FREECAD ASSEMBLY — COMPONENT RECIPES ("XL30AssemblyChamber01")

This assembly document has 18 components, labeled P0..P17 below (a component is one placed body or linked part). 3 of them carry a construction recipe — the FreeCAD feature program that regenerates the part from scratch, quoted from this document or its linked companion documents; the rest are supplied as boundary geometry only. No exploded tour is included for this assembly.
COMPONENT P0 — geometry summary ("PortAligner_BoughtExternally"; no construction recipe available for this part):
  bounding box: 138.3 x 135.3 x 130.5 mm
  tessellated surface: 227,052 triangles
  volume: 334006 mm^3 (14% of its bounding box)
COMPONENT P1 — recipe-attached ("MainChamberModel", a linked part whose construction recipe lives in a companion FreeCAD document of the same project; that document's serialized recipe follows).
Construction recipe (the companion document, serialized — sketch geometry with constraints, then the solid features built on it; lengths are millimeters unless a unit is written):

FCSTD DOCUMENT  (FreeCAD 0.20R)
Label: XL30MainChamberModel
License: All rights reserved
LicenseURL: http://en.wikipedia.org/wiki/All_rights_reserved
objects: Part::Cylinder×49, Part::Cut×21, Part::Compound×17, Part::MultiFuse×8, Part::Box×7, Part::Sphere×1
note: 103 computed .brp shape members not serialized (recipe doc carries the construction recipe); baked Part::Feature solids carry a one-line shape summary decoded from their .brp

FEATURE [Part::Box] Box  label="Würfel"
  AttacherType = Attacher::AttachEngine3D
  Height = 330
  Length = 330
  Width = 180
FEATURE [Part::Cylinder] Cylinder  label="Zylinder"
  Angle = 360
  AttacherType = Attacher::AttachEngine3D
  FirstAngle = 0
  Height = 180
  Placement = pos=(165,180,165) rot=(1,0,0;1.5708rad)
  Radius = 142
  SecondAngle = 0
FEATURE [Part::Cut] Cut
  Base = -> Box
  Tool = -> Cylinder
FEATURE [Part::Box] Box001  label="Würfel001"
  AttacherType = Attacher::AttachEngine3D
  Height = 50
  Length = 70
  Placement = pos=(0,0,265) rot=(0,-1,0;1.20428rad)
  Width = 180
FEATURE [Part::Cut] Cut001
  Base = -> Cut
  Tool = -> Box001
FEATURE [Part::Cylinder] Cylinder001  label="Flange100Right_Hole"
  Angle = 360
  AttacherType = Attacher::AttachEngine3D
  FirstAngle = 0
  Height = 50
  Placement = pos=(284,107.5,198.5) rot=(0,1,0;1.5708rad)
  Radius = 34.5
  SecondAngle = 0
FEATURE [Part::Cylinder] Cylinder002  label="Flange100Right_Recess"
  Angle = 360
  AttacherType = Attacher::AttachEngine3D
  FirstAngle = 0
  Height = 1
  Placement = pos=(329,107.5,198.5) rot=(0,1,0;1.5708rad)
  Radius = 51.5
  SecondAngle = 0
FEATURE [Part::Cylinder] Cylinder003  label="Zylinder001"
  Angle = 360
  AttacherType = Attacher::AttachEngine3D
  FirstAngle = 0
  Height = 3
  Radius = 41
  SecondAngle = 0
FEATURE [Part::Cylinder] Cylinder004  label="Zylinder002"
  Angle = 360
  AttacherType = Attacher::AttachEngine3D
  FirstAngle = 0
  Height = 3
  Radius = 37
  SecondAngle = 0
FEATURE [Part::Cut] Cut002
  Base = -> Cylinder003
  Placement = pos=(326,107.5,198.5) rot=(0,1,0;1.5708rad)
  Tool = -> Cylinder004
FEATURE [Part::Cylinder] Cylinder005  label="Zylinder003"
  Angle = 360
  AttacherType = Attacher::AttachEngine3D
  FirstAngle = 0
  Height = 10
  Placement = pos=(0,0,-44.3) rot=(0,1,0;1.5708rad)
  Radius = 1.65
  SecondAngle = 0
FEATURE [Part::Cylinder] Cylinder006  label="Zylinder004"
  Angle = 360
  AttacherType = Attacher::AttachEngine3D
  FirstAngle = 0
  Height = 10
  Placement = pos=(0,0,-44.3) rot=(0,1,0;1.5708rad)
  Radius = 1.65
  SecondAngle = 0
FEATURE [Part::Cylinder] Cylinder007  label="Zylinder005"
  Angle = 360
  AttacherType = Attacher::AttachEngine3D
  FirstAngle = 0
  Height = 10
  Placement = pos=(0,0,-44.3) rot=(0,1,0;1.5708rad)
  Radius = 1.65
  SecondAngle = 0
FEATURE [Part::Compound] Compound001
  Links = -> [Cylinder006]
  Placement = pos=(0,0,0) rot=(1,0,0;2.0944rad)
FEATURE [Part::Compound] Compound002
  Links = -> [Cylinder007]
  Placement = pos=(0,0,0) rot=(1,0,0;4.18879rad)
FEATURE [Part::Compound] Compound003  label="M4 holes flange right"
  Links = -> [Cylinder005,Compound001,Compound002]
  Placement = pos=(319,107.5,198.5) rot=(0,0,1;0rad)
FEATURE [Part::MultiFuse] Fusion
  Shapes = -> [Cylinder001,Cylinder002,Cut002,Compound003]
FEATURE [Part::Cut] Cut003
  Base = -> Cut001
  Tool = -> Fusion
FEATURE [Part::Cylinder] Cylinder008  label="Flange120LeftLow_Recess"
  Angle = 360
  AttacherType = Attacher::AttachEngine3D
  FirstAngle = 0
  Height = 1
  Placement = pos=(0,0,-1) rot=(0,0,1;0rad)
  Radius = 61.5
  SecondAngle = 0
FEATURE [Part::Cylinder] Cylinder009  label="Zylinder006"
  Angle = 360
  AttacherType = Attacher::AttachEngine3D
  FirstAngle = 0
  Height = 60
  Placement = pos=(0,0,-45) rot=(0,0,1;0rad)
  Radius = 45
  SecondAngle = 0
FEATURE [Part::Cylinder] Cylinder010  label="Zylinder007"
  Angle = 360
  AttacherType = Attacher::AttachEngine3D
  FirstAngle = 0
  Height = 2
  Placement = pos=(0,0,-3) rot=(0,0,1;0rad)
  Radius = 50
  SecondAngle = 0
FEATURE [Part::Cylinder] Cylinder011  label="Zylinder008"
  Angle = 360
  AttacherType = Attacher::AttachEngine3D
  FirstAngle = 0
  Height = 2
  Placement = pos=(0,0,-3) rot=(0,0,1;0rad)
  Radius = 46
  SecondAngle = 0
FEATURE [Part::Cut] Cut004
  Base = -> Cylinder010
  Tool = -> Cylinder011
FEATURE [Part::Cylinder] Cylinder012  label="Zylinder009"
  Angle = 360
  AttacherType = Attacher::AttachEngine3D
  FirstAngle = 0
  Height = 10
  Placement = pos=(54.5,0,-10) rot=(0,0,1;0rad)
  Radius = 2.5
  SecondAngle = 0
FEATURE [Part::Cylinder] Cylinder013  label="Zylinder010"
  Angle = 360
  AttacherType = Attacher::AttachEngine3D
  FirstAngle = 0
  Height = 10
  Placement = pos=(54.5,0,-10) rot=(0,0,1;0rad)
  Radius = 2.5
  SecondAngle = 0
FEATURE [Part::Cylinder] Cylinder015  label="Zylinder012"
  Angle = 360
  AttacherType = Attacher::AttachEngine3D
  FirstAngle = 0
  Height = 10
  Placement = pos=(54.5,0,-10) rot=(0,0,1;0rad)
  Radius = 2.5
  SecondAngle = 0
FEATURE [Part::Compound] Compound
  Links = -> [Cylinder013]
  Placement = pos=(0,0,0) rot=(0,0,1;2.0944rad)
FEATURE [Part::Compound] Compound004
  Links = -> [Cylinder015]
  Placement = pos=(0,0,0) rot=(0,0,1;4.18879rad)
FEATURE [Part::MultiFuse] Fusion001  label="Flange120LeftLow"
  Placement = pos=(0,115.5,140) rot=(0,-1,0;1.5708rad)
  Shapes = -> [Cylinder008,Cylinder009,Cut004,Cylinder012,Compound,Compound004]
FEATURE [Part::Cut] Cut005
  Base = -> Cut003
  Tool = -> Fusion001
FEATURE [Part::Cylinder] Cylinder016  label="Zylinder013"
  Angle = 360
  AttacherType = Attacher::AttachEngine3D
  FirstAngle = 0
  Height = 100
  Placement = pos=(0,0,0) rot=(0,1,0;1.5708rad)
  Radius = 27
  SecondAngle = 0
FEATURE [Part::Cylinder] Cylinder017  label="Zylinder014"
  Angle = 360
  AttacherType = Attacher::AttachEngine3D
  FirstAngle = 0
  Height = 100
  Placement = pos=(-99,0,0) rot=(0,1,0;1.5708rad)
  Radius = 51.5
  SecondAngle = 0
FEATURE [Part::Cylinder] Cylinder018  label="Zylinder015"
  Angle = 360
  AttacherType = Attacher::AttachEngine3D
  FirstAngle = 0
  Height = 2
  Radius = 41
  SecondAngle = 0
FEATURE [Part::Cylinder] Cylinder019  label="Zylinder016"
  Angle = 360
  AttacherType = Attacher::AttachEngine3D
  FirstAngle = 0
  Height = 2
  Radius = 37
  SecondAngle = 0
FEATURE [Part::Cut] Cut006
  Base = -> Cylinder018
  Placement = pos=(1,0,0) rot=(0,1,0;1.5708rad)
  Tool = -> Cylinder019
FEATURE [Part::Cylinder] Cylinder020  label="Zylinder017"
  Angle = 360
  AttacherType = Attacher::AttachEngine3D
  FirstAngle = 0
  Height = 10
  Placement = pos=(0,0,-44.5) rot=(0,1,0;1.5708rad)
  Radius = 3.3
  SecondAngle = 0
FEATURE [Part::Cylinder] Cylinder021  label="Zylinder018"
  Angle = 360
  AttacherType = Attacher::AttachEngine3D
  FirstAngle = 0
  Height = 10
  Placement = pos=(0,0,-44.5) rot=(0,1,0;1.5708rad)
  Radius = 3.3
  SecondAngle = 0
FEATURE [Part::Cylinder] Cylinder022  label="Zylinder019"
  Angle = 360
  AttacherType = Attacher::AttachEngine3D
  FirstAngle = 0
  Height = 10
  Placement = pos=(0,0,-44.5) rot=(0,1,0;1.5708rad)
  Radius = 3.3
  SecondAngle = 0
FEATURE [Part::Compound] Compound005
  Links = -> [Cylinder021]
  Placement = pos=(0,0,0) rot=(1,0,0;2.0944rad)
FEATURE [Part::Compound] Compound006
  Links = -> [Cylinder022]
  Placement = pos=(0,0,0) rot=(1,0,0;4.18879rad)
FEATURE [Part::MultiFuse] Fusion002  label="FlangeSEDetector"
  Placement = pos=(18,116,275) rot=(0,1,0;0.340339rad)
  Shapes = -> [Cylinder016,Cylinder017,Cut006,Cylinder020,Compound005,Compound006]
FEATURE [Part::Cut] Cut007
  Base = -> Cut005
  Tool = -> Fusion002
FEATURE [Part::Cylinder] Cylinder023  label="ODPHoleNoFlange"
  Angle = 360
  AttacherType = Attacher::AttachEngine3D
  FirstAngle = 0
  Height = 50
  Placement = pos=(125,140,0) rot=(0,0,1;0rad)
  Radius = 40
  SecondAngle = 0
FEATURE [Part::Cut] Cut008
  Base = -> Cut007
  Tool = -> Cylinder023
FEATURE [Part::Cylinder] Cylinder024  label="EGunHoleWithoutFlange"
  Angle = 360
  AttacherType = Attacher::AttachEngine3D
  FirstAngle = 0
  Height = 50
  Placement = pos=(165,120,280) rot=(0,0,1;0rad)
  Radius = 50
  SecondAngle = 0
FEATURE [Part::Cut] Cut009  label="FrontChamber"
  Base = -> Cut008
  Tool = -> Cylinder024
FEATURE [Part::Box] Box002  label="Würfel002"
  AttacherType = Attacher::AttachEngine3D
  Height = 330
  Length = 330
  Width = 105
FEATURE [Part::Box] Box003  label="Würfel003"
  AttacherType = Attacher::AttachEngine3D
  Height = 330
  Length = 150
  Placement = pos=(330,0,0) rot=(0,0,1;0.785398rad)
  Width = 200
FEATURE [Part::Box] Box004  label="Würfel004"
  AttacherType = Attacher::AttachEngine3D
  Height = 150
  Length = 240
  Placement = pos=(90,0,330) rot=(-1,0,0;0.785398rad)
  Width = 150
FEATURE [Part::Box] Box005  label="Würfel005"
  AttacherType = Attacher::AttachEngine3D
  Height = 330
  Length = 150
  Placement = pos=(0,15,0) rot=(0,0,1;0.785398rad)
  Width = 100
FEATURE [Part::Box] Box007  label="Würfel007"
  AttacherType = Attacher::AttachEngine3D
  Height = 50
  Length = 70
  Placement = pos=(0,0,265) rot=(0,-1,0;1.20428rad)
  Width = 180
FEATURE [Part::MultiFuse] Fusion003
  Shapes = -> [Box005,Box003,Box004,Box007]
FEATURE [Part::Cut] Cut010
  Base = -> Box002
  Placement = pos=(0,180,0) rot=(0,0,1;0rad)
  Tool = -> Fusion003
FEATURE [Part::Cylinder] Cylinder025  label="Zylinder020"
  Angle = 360
  AttacherType = Attacher::AttachEngine3D
  FirstAngle = 0
  Height = 100
  Placement = pos=(0,0,0) rot=(0,1,0;1.5708rad)
  Radius = 27
  SecondAngle = 0
FEATURE [Part::Cylinder] Cylinder026  label="Zylinder021"
  Angle = 360
  AttacherType = Attacher::AttachEngine3D
  FirstAngle = 0
  Height = 100
  Placement = pos=(-99,0,0) rot=(0,1,0;1.5708rad)
  Radius = 51.5
  SecondAngle = 0
FEATURE [Part::Cylinder] Cylinder027  label="Zylinder022"
  Angle = 360
  AttacherType = Attacher::AttachEngine3D
  FirstAngle = 0
  Height = 2
  Radius = 41
  SecondAngle = 0
FEATURE [Part::Cylinder] Cylinder028  label="Zylinder023"
  Angle = 360
  AttacherType = Attacher::AttachEngine3D
  FirstAngle = 0
  Height = 2
  Radius = 37
  SecondAngle = 0
FEATURE [Part::Cut] Cut011
  Base = -> Cylinder027
  Placement = pos=(1,0,0) rot=(0,1,0;1.5708rad)
  Tool = -> Cylinder028
FEATURE [Part::Cylinder] Cylinder029  label="Zylinder024"
  Angle = 360
  AttacherType = Attacher::AttachEngine3D
  FirstAngle = 0
  Height = 10
  Placement = pos=(0,0,-44.5) rot=(0,1,0;1.5708rad)
  Radius = 3.3
  SecondAngle = 0
FEATURE [Part::Cylinder] Cylinder030  label="Zylinder025"
  Angle = 360
  AttacherType = Attacher::AttachEngine3D
  FirstAngle = 0
  Height = 10
  Placement = pos=(0,0,-44.5) rot=(0,1,0;1.5708rad)
  Radius = 3.3
  SecondAngle = 0
FEATURE [Part::Compound] Compound007
  Links = -> [Cylinder030]
  Placement = pos=(0,0,0) rot=(1,0,0;2.0944rad)
FEATURE [Part::Cylinder] Cylinder031  label="Zylinder026"
  Angle = 360
  AttacherType = Attacher::AttachEngine3D
  FirstAngle = 0
  Height = 10
  Placement = pos=(0,0,-44.5) rot=(0,1,0;1.5708rad)
  Radius = 3.3
  SecondAngle = 0
FEATURE [Part::Compound] Compound008
  Links = -> [Cylinder031]
  Placement = pos=(0,0,0) rot=(1,0,0;4.18879rad)
FEATURE [Part::MultiFuse] Fusion004  label="BSEFlange"
  Placement = pos=(278.7,231.3,105) rot=(0,0,1;3.92699rad)
  Shapes = -> [Cylinder025,Cylinder026,Cut011,Cylinder029,Compound007,Compound008]
FEATURE [Part::Compound] Compound009  label="BSEFlange1"
  Links = -> [Fusion004]
FEATURE [Part::Cut] Cut012
  Base = -> Cut010
  Tool = -> Compound009
FEATURE [Part::Cylinder] Cylinder032  label="Zylinder027"
  Angle = 360
  AttacherType = Attacher::AttachEngine3D
  FirstAngle = 0
  Height = 100
  Placement = pos=(0,0,0) rot=(0,1,0;1.5708rad)
  Radius = 20
  SecondAngle = 0
FEATURE [Part::Cylinder] Cylinder033  label="Zylinder028"
  Angle = 360
  AttacherType = Attacher::AttachEngine3D
  FirstAngle = 0
  Height = 100
  Placement = pos=(-99,0,0) rot=(0,1,0;1.5708rad)
  Radius = 44
  SecondAngle = 0
FEATURE [Part::Cylinder] Cylinder034  label="Zylinder029"
  Angle = 360
  AttacherType = Attacher::AttachEngine3D
  FirstAngle = 0
  Height = 2
  Radius = 33.8
  SecondAngle = 0
FEATURE [Part::Cylinder] Cylinder035  label="Zylinder030"
  Angle = 360
  AttacherType = Attacher::AttachEngine3D
  FirstAngle = 0
  Height = 2
  Radius = 30
  SecondAngle = 0
FEATURE [Part::Cut] Cut013
  Base = -> Cylinder034
  Placement = pos=(1,0,0) rot=(0,1,0;1.5708rad)
  Tool = -> Cylinder035
FEATURE [Part::Cylinder] Cylinder036  label="Zylinder031"
  Angle = 360
  AttacherType = Attacher::AttachEngine3D
  FirstAngle = 0
  Height = 10
  Placement = pos=(0,0,-37.5) rot=(0,1,0;1.5708rad)
  Radius = 3.3
  SecondAngle = 0
FEATURE [Part::Cylinder] Cylinder037  label="Zylinder032"
  Angle = 360
  AttacherType = Attacher::AttachEngine3D
  FirstAngle = 0
  Height = 10
  Placement = pos=(0,0,-37.5) rot=(0,1,0;1.5708rad)
  Radius = 3.3
  SecondAngle = 0
FEATURE [Part::Compound] Compound010
  Links = -> [Cylinder037]
  Placement = pos=(0,0,0) rot=(1,0,0;2.0944rad)
FEATURE [Part::Cylinder] Cylinder038  label="Zylinder033"
  Angle = 360
  AttacherType = Attacher::AttachEngine3D
  FirstAngle = 0
  Height = 10
  Placement = pos=(0,0,-37.5) rot=(0,1,0;1.5708rad)
  Radius = 3.3
  SecondAngle = 0
FEATURE [Part::Compound] Compound011
  Links = -> [Cylinder038]
  Placement = pos=(0,0,0) rot=(1,0,0;4.18879rad)
FEATURE [Part::MultiFuse] Fusion005  label="BSEFlange003"
  Placement = pos=(0,0,0) rot=(0,0,-1;0.785398rad)
  Shapes = -> [Cylinder032,Cylinder033,Cut013,Cylinder036,Compound010,Compound011]
FEATURE [Part::Compound] Compound012  label="SideFlangeBack2Low"
  Links = -> [Fusion005]
  Placement = pos=(45,240,97.5) rot=(0,0,1;0rad)
FEATURE [Part::Cut] Cut014
  Base = -> Cut012
  Tool = -> Compound012
FEATURE [Part::Cylinder] Cylinder039  label="Zylinder034"
  Angle = 360
  AttacherType = Attacher::AttachEngine3D
  FirstAngle = 0
  Height = 110
  Placement = pos=(-20,0,20) rot=(0,1,0;2.35619rad)
  Radius = 20
  SecondAngle = 0
FEATURE [Part::Cylinder] Cylinder040  label="Zylinder035"
  Angle = 360
  AttacherType = Attacher::AttachEngine3D
  FirstAngle = 0
  Height = 100
  Placement = pos=(-99,0,0) rot=(0,1,0;1.5708rad)
  Radius = 51.5
  SecondAngle = 0
FEATURE [Part::Cylinder] Cylinder041  label="Zylinder036"
  Angle = 360
  AttacherType = Attacher::AttachEngine3D
  FirstAngle = 0
  Height = 2
  Radius = 41
  SecondAngle = 0
FEATURE [Part::Cylinder] Cylinder042  label="Zylinder037"
  Angle = 360
  AttacherType = Attacher::AttachEngine3D
  FirstAngle = 0
  Height = 2
  Radius = 37
  SecondAngle = 0
FEATURE [Part::Cut] Cut015
  Base = -> Cylinder041
  Placement = pos=(1,0,0) rot=(0,1,0;1.5708rad)
  Tool = -> Cylinder042
FEATURE [Part::Cylinder] Cylinder043  label="Zylinder038"
  Angle = 360
  AttacherType = Attacher::AttachEngine3D
  FirstAngle = 0
  Height = 10
  Placement = pos=(0,0,-44.5) rot=(0,1,0;1.5708rad)
  Radius = 3.3
  SecondAngle = 0
FEATURE [Part::Cylinder] Cylinder044  label="Zylinder039"
  Angle = 360
  AttacherType = Attacher::AttachEngine3D
  FirstAngle = 0
  Height = 10
  Placement = pos=(0,0,-44.5) rot=(0,1,0;1.5708rad)
  Radius = 3.3
  SecondAngle = 0
FEATURE [Part::Compound] Compound013
  Links = -> [Cylinder044]
  Placement = pos=(0,0,0) rot=(1,0,0;2.0944rad)
FEATURE [Part::Cylinder] Cylinder045  label="Zylinder040"
  Angle = 360
  AttacherType = Attacher::AttachEngine3D
  FirstAngle = 0
  Height = 10
  Placement = pos=(0,0,-44.5) rot=(0,1,0;1.5708rad)
  Radius = 3.3
  SecondAngle = 0
FEATURE [Part::Compound] Compound014
  Links = -> [Cylinder045]
  Placement = pos=(0,0,0) rot=(1,0,0;4.18879rad)
FEATURE [Part::MultiFuse] Fusion006  label="BSEFlange005"
  Placement = pos=(0,0,286) rot=(0,0,-1;0.785398rad)
  Shapes = -> [Cylinder039,Cylinder040,Cut015,Cylinder043,Compound013,Compound014]
FEATURE [Part::Compound] Compound015  label="BackTopFlange100"
  Links = -> [Fusion006]
  Placement = pos=(45,240,0) rot=(0,0,1;0rad)
FEATURE [Part::Cut] Cut016  label="BackChamber01"
  Base = -> Cut014
  Tool = -> Compound015
FEATURE [Part::Cylinder] Cylinder046  label="Zylinder041"
  Angle = 360
  AttacherType = Attacher::AttachEngine3D
  FirstAngle = 0
  Height = 800
  Placement = pos=(36,500,38) rot=(1,0,0;1.5708rad)
  Radius = 10
  SecondAngle = 0
FEATURE [Part::Cylinder] Cylinder047  label="Zylinder042"
  Angle = 360
  AttacherType = Attacher::AttachEngine3D
  FirstAngle = 0
  Height = 800
  Placement = pos=(302,500,34) rot=(1,0,0;1.5708rad)
  Radius = 10
  SecondAngle = 0
FEATURE [Part::Compound] Compound016
  Links = -> [Cylinder047,Cylinder046]
FEATURE [Part::Sphere] Sphere  label="Kugel"
  Angle1 = -90
  Angle2 = 90
  Angle3 = 360
  AttacherType = Attacher::AttachEngine3D
  Placement = pos=(165,0,165) rot=(0,0,1;0rad)
  Radius = 230
FEATURE [Part::Cut] Cut017
  Base = -> Cut016
  Tool = -> Sphere
FEATURE [Part::MultiFuse] Fusion007
  Shapes = -> [Cut009,Cut017]
FEATURE [Part::Cut] Cut018
  Base = -> Fusion007
  Tool = -> Compound016
FEATURE [Part::Cylinder] Cylinder048  label="Zylinder043"
  Angle = 360
  AttacherType = Attacher::AttachEngine3D
  FirstAngle = 0
  Height = 4
  Radius = 155
  SecondAngle = 0
FEATURE [Part::Cylinder] Cylinder049  label="Zylinder044"
  Angle = 360
  AttacherType = Attacher::AttachEngine3D
  FirstAngle = 0
  Height = 4
  Radius = 151
  SecondAngle = 0
FEATURE [Part::Cut] Cut019
  Base = -> Cylinder048
  Placement = pos=(165,4,165) rot=(1,0,0;1.5708rad)
  Tool = -> Cylinder049
FEATURE [Part::Cut] Cut020  label="MainChamberModel"
  Base = -> Cut018
  Tool = -> Cut019
COMPONENT P2 — geometry summary ("BasicOutline_Part0and1"; no construction recipe available for this part):
  bounding box: 150.0 x 150.0 x 137.0 mm
  tessellated surface: 6,006 triangles
  volume: 950630 mm^3 (31% of its bounding box)
  symmetry: 4-fold rotationally symmetric about the z axis; mirror-symmetric across its x mid-plane, y mid-plane
COMPONENT P3 — recipe-attached ("XL30FinalAppertureHolder", a linked part whose construction recipe lives in a companion FreeCAD document of the same project; that document's serialized recipe follows).
Construction recipe (the companion document, serialized — sketch geometry with constraints, then the solid features built on it; lengths are millimeters unless a unit is written):

FCSTD DOCUMENT  (FreeCAD 0.20R)
Label: XL30FinalAppertureHolder
License: All rights reserved
LicenseURL: http://en.wikipedia.org/wiki/All_rights_reserved
objects: Part::Cylinder×8, Part::MultiFuse×2, Part::Cut×2, PartDesign::AdditiveCylinder×1, PartDesign::Hole×1, PartDesign::Body×1, Part::Feature×1
note: 18 computed .brp shape members not serialized (recipe doc carries the construction recipe); baked Part::Feature solids carry a one-line shape summary decoded from their .brp

FEATURE [Part::Cylinder] Cylinder  label="Zylinder"
  Angle = 360
  AttacherType = Attacher::AttachEngine3D
  FirstAngle = 0
  Height = 0.5
  Radius = 4.5
  SecondAngle = 0
FEATURE [Part::Cylinder] Cylinder001  label="Zylinder001"
  Angle = 360
  AttacherType = Attacher::AttachEngine3D
  FirstAngle = 0
  Height = 0.9
  Radius = 3.5
  SecondAngle = 0
FEATURE [Part::Cylinder] Cylinder002  label="Zylinder002"
  Angle = 360
  AttacherType = Attacher::AttachEngine3D
  FirstAngle = 0
  Height = 3.5
  Radius = 2.5
  SecondAngle = 0
FEATURE [Part::Cylinder] Cylinder003  label="Zylinder003"
  Angle = 360
  AttacherType = Attacher::AttachEngine3D
  FirstAngle = 0
  Height = 4
  Placement = pos=(0,0,3.5) rot=(0,0,1;0rad)
  Radius = 2.4
  SecondAngle = 0
FEATURE [Part::Cylinder] Cylinder004  label="Zylinder004"
  Angle = 360
  AttacherType = Attacher::AttachEngine3D
  FirstAngle = 0
  Height = 10
  Radius = 1.87
  SecondAngle = 0
FEATURE [Part::MultiFuse] Fusion
  Shapes = -> [Cylinder004,Cylinder,Cylinder001,Cylinder002,Cylinder003]
FEATURE [Part::Cylinder] Cylinder005  label="Zylinder005"
  Angle = 360
  AttacherType = Attacher::AttachEngine3D
  FirstAngle = 0
  Height = 100
  Radius = 1.2
  SecondAngle = 0
FEATURE [Part::Cylinder] Cylinder006  label="Zylinder006"
  Angle = 360
  AttacherType = Attacher::AttachEngine3D
  FirstAngle = 0
  Height = 7
  Radius = 2
  SecondAngle = 0
FEATURE [Part::Cylinder] Cylinder007  label="Zylinder007"
  Angle = 360
  AttacherType = Attacher::AttachEngine3D
  FirstAngle = 0
  Height = 10
  Placement = pos=(0,0,8) rot=(0,0,1;0rad)
  Radius = 1.5
  SecondAngle = 0
FEATURE [Part::MultiFuse] Fusion001
  Shapes = -> [Cylinder007,Cylinder005,Cylinder006]
FEATURE [Part::Cut] Cut
  Base = -> Fusion
  Tool = -> Fusion001
FEATURE [PartDesign::AdditiveCylinder] Cylinder008
  Angle = 360
  AttacherType = Attacher::AttachEngine3D
  FirstAngle = 0
  Height = 4
  Radius = 3
  SecondAngle = 0
FEATURE [PartDesign::Hole] Hole
  BaseFeature = -> Cylinder008
  CustomThreadClearance = 0
  Depth = 18.9163
  DepthType = 0
  Diameter = 4.224
  DrillForDepth = false
  DrillPoint = 1
  DrillPointAngle = 118
  HoleCutCountersinkAngle = 90
  HoleCutCustomValues = false
  HoleCutDepth = 0
  HoleCutDiameter = 6.1
  HoleCutType = 0
  ModelThread = true
  Profile = -> Cylinder008 [Face3]
  Tapered = false
  TaperedAngle = 90
  ThreadClass = 0
  ThreadDepth = 18.9163
  ThreadDepthType = 0
  ThreadDirection = 0
  ThreadFit = 0
  ThreadSize = 13
  ThreadType = 1
  Threaded = true
  UseCustomThreadClearance = false
FEATURE [PartDesign::Body] Body  label="ThreadCutterM3"
  Group = -> [Cylinder008,Hole]
  Origin = -> Origin
  Placement = pos=(0,0,3.5) rot=(0,0,1;0rad)
  Tip = -> Hole
FEATURE [Part::Cut] Cut001
  Base = -> Cut
  Tool = -> Body
FEATURE [Part::Feature] Cut001_solid  label="XL30FinalAppertureHolder"
  shape: bbox 9 x 9 x 10 mm, 44 faces (baked)
COMPONENT P4 — geometry summary ("AttachmentRing_Column01"; no construction recipe available for this part):
  bounding box: 115.3 x 115.3 x 5.0 mm
  tessellated surface: 12,346 triangles
  volume: 12698 mm^3 (19% of its bounding box)
  symmetry: 2-fold rotationally symmetric about the x axis; 4-fold rotationally symmetric about the z axis; mirror-symmetric across its x mid-plane, y mid-plane, z mid-plane
COMPONENT P5 — geometry summary ("Stackmountring01"; no construction recipe available for this part):
  bounding box: 115.3 x 115.3 x 5.0 mm
  tessellated surface: 3,520 triangles
  volume: 15095 mm^3 (23% of its bounding box)
  symmetry: 2-fold rotationally symmetric about the z axis; mirror-symmetric across its x mid-plane, y mid-plane
COMPONENT P6 — geometry summary ("PCBStackTemplate"; no construction recipe available for this part):
  bounding box: 42.0 x 40.0 x 20.0 mm
  tessellated surface: 788 triangles
  volume: 32924 mm^3 (98% of its bounding box)
  symmetry: 2-fold rotationally symmetric about the x axis; mirror-symmetric across its y mid-plane, z mid-plane
COMPONENT P7 — geometry summary ("StageAssembly"; no construction recipe available for this part):
  bounding box: 82.0 x 61.0 x 43.0 mm
  tessellated surface: 7,384 triangles
  volume: 51070 mm^3 (24% of its bounding box)
  symmetry: mirror-symmetric across its y mid-plane
COMPONENT P8 — geometry summary ("XL30FrontdoorCF64Flanges (Solid)"; no construction recipe available for this part):
  bounding box: 330.0 x 330.0 x 35.0 mm
  tessellated surface: 23,184 triangles
  volume: 2510343 mm^3 (66% of its bounding box)
COMPONENT P9 — geometry summary ("StageAssembly001"; no construction recipe available for this part):
  bounding box: 82.0 x 61.0 x 43.0 mm
  tessellated surface: 7,384 triangles
  volume: 51070 mm^3 (24% of its bounding box)
  symmetry: mirror-symmetric across its y mid-plane
COMPONENT P10 — geometry summary ("StageAssembly003"; no construction recipe available for this part):
  bounding box: 82.0 x 61.0 x 43.0 mm
  tessellated surface: 7,384 triangles
  volume: 51070 mm^3 (24% of its bounding box)
  symmetry: mirror-symmetric across its x mid-plane
COMPONENT P11 — geometry summary ("Flange100mmToCF40_Right"; no construction recipe available for this part):
  bounding box: 100.0 x 100.0 x 17.3 mm
  tessellated surface: 10,594 triangles
  volume: 85223 mm^3 (49% of its bounding box)
  symmetry: 3-fold rotationally symmetric about the x axis; mirror-symmetric across its y mid-plane
COMPONENT P12 — geometry summary ("Cut017"; no construction recipe available for this part):
  bounding box: 120.0 x 120.0 x 28.5 mm
  tessellated surface: 14,928 triangles
  volume: 174689 mm^3 (43% of its bounding box)
COMPONENT P13 — geometry summary ("Flange85mmToCF40_BackBottom_001"; no construction recipe available for this part):
  bounding box: 85.0 x 85.0 x 17.3 mm
  tessellated surface: 10,676 triangles
  volume: 59456 mm^3 (48% of its bounding box)
  symmetry: 3-fold rotationally symmetric about the x axis; mirror-symmetric across its y mid-plane
COMPONENT P14 — geometry summary ("XL30TopBackFlange100"; no construction recipe available for this part):
  bounding box: 100.0 x 94.0 x 12.0 mm
  tessellated surface: 3,748 triangles
  volume: 87641 mm^3 (78% of its bounding box)
  symmetry: mirror-symmetric across its x mid-plane
COMPONENT P15 — geometry summary ("KickerAssembly"; no construction recipe available for this part):
  bounding box: 44.0 x 43.0 x 42.0 mm
  tessellated surface: 9,350 triangles
  volume: 9360 mm^3 (12% of its bounding box)
COMPONENT P16 — geometry summary ("AligningRing (Solid)"; no construction recipe available for this part):
  bounding box: 48.0 x 48.0 x 5.0 mm
  tessellated surface: 6,060 triangles
  volume: 5171 mm^3 (45% of its bounding box)
  symmetry: mirror-symmetric across its y mid-plane
COMPONENT P17 — recipe-attached ("Kickeraligner (Solid)", a linked part whose construction recipe lives in a companion FreeCAD document of the same project; that document's serialized recipe follows).
Construction recipe (the companion document, serialized — sketch geometry with constraints, then the solid features built on it; lengths are millimeters unless a unit is written):

FCSTD DOCUMENT  (FreeCAD 0.22R0.21.2)
Label: PhilipsXL30_AligningRing
License: All rights reserved
LicenseURL: http://en.wikipedia.org/wiki/All_rights_reserved
objects: TechDraw::DrawViewDimension×43, Part::Cylinder×18, Part::MultiFuse×9, TechDraw::DrawProjGroupItem×8, Part::Cut×7, Part::Box×5, Part::FeaturePython×3, TechDraw::DrawSVGTemplate×3, TechDraw::DrawViewSection×3, TechDraw::DrawPage×3, Part::Feature×2, TechDraw::DrawProjGroup×2, TechDraw::DrawViewPart×2, Part::Cone×1
note: 107 computed .brp shape members not serialized (recipe doc carries the construction recipe); baked Part::Feature solids carry a one-line shape summary decoded from their .brp

FEATURE [Part::Cone] Cone001
  Angle = 360
  AttacherType = Attacher::AttachEngine3D
  Height = 20
  Placement = pos=(0,0,-5) rot=(0,0,1;0rad)
  Radius1 = 6.5
  Radius2 = 26.5
FEATURE [Part::Cylinder] Cylinder
  Angle = 360
  AttacherType = Attacher::AttachEngine3D
  FirstAngle = 0
  Height = 5
  Radius = 24
  SecondAngle = 0
FEATURE [Part::Cut] Cut
  Base = -> Cylinder
  Tool = -> Cone001
FEATURE [Part::Box] Box  label="Cube"
  AttacherType = Attacher::AttachEngine3D
  Height = 25
  Length = 5
  Placement = pos=(3.5,-22,-25) rot=(0,0,1;0rad)
  Width = 44
FEATURE [Part::Cylinder] Cylinder001
  Angle = 360
  AttacherType = Attacher::AttachEngine3D
  FirstAngle = 0
  Height = 10
  Radius = 1.2
  SecondAngle = 0
FEATURE [Part::Cylinder] Cylinder002
  Angle = 360
  AttacherType = Attacher::AttachEngine3D
  FirstAngle = 0
  Height = 10
  Placement = pos=(12.6,0,0) rot=(0,0,1;0rad)
  Radius = 1.2
  SecondAngle = 0
FEATURE [Part::Box] Box001  label="Cube001"
  AttacherType = Attacher::AttachEngine3D
  Height = 10
  Length = 12.5
  Placement = pos=(0,-1.2,0) rot=(0,0,1;0rad)
  Width = 2.4
FEATURE [Part::MultiFuse] Fusion  label="Langloch"
  Placement = pos=(0,5.75,-7.7) rot=(0,1,0;1.5708rad)
  Shapes = -> [Box001,Cylinder001,Cylinder002]
FEATURE [Part::Box] Box002  label="Cube002"
  AttacherType = Attacher::AttachEngine3D
  Height = 10
  Length = 12.5
  Placement = pos=(0,-1.2,0) rot=(0,0,1;0rad)
  Width = 2.4
FEATURE [Part::Cylinder] Cylinder003
  Angle = 360
  AttacherType = Attacher::AttachEngine3D
  FirstAngle = 0
  Height = 10
  Radius = 1.2
  SecondAngle = 0
FEATURE [Part::Cylinder] Cylinder004
  Angle = 360
  AttacherType = Attacher::AttachEngine3D
  FirstAngle = 0
  Height = 10
  Placement = pos=(12.6,0,0) rot=(0,0,1;0rad)
  Radius = 1.2
  SecondAngle = 0
FEATURE [Part::MultiFuse] Fusion001  label="Langloch001"
  Placement = pos=(0,-5.75,-7.7) rot=(0,1,0;1.5708rad)
  Shapes = -> [Box002,Cylinder003,Cylinder004]
FEATURE [Part::MultiFuse] Fusion002
  Shapes = -> [Fusion001,Fusion]
FEATURE [Part::Cut] Cut001
  Base = -> Box
  Tool = -> Fusion002
FEATURE [Part::Cylinder] Cylinder005
  Angle = 360
  AttacherType = Attacher::AttachEngine3D
  FirstAngle = 0
  Height = 17
  Placement = pos=(0,0,-6) rot=(0,0,1;0rad)
  Radius = 12
  SecondAngle = 0
FEATURE [Part::Cut] Cut002
  Base = -> Cut001
  Tool = -> Cylinder005
FEATURE [Part::FeaturePython] Screw  label="M3x8-Screw"  # Fasteners workbench fastener (typed FeaturePython)
  Placement = pos=(6,19,3) rot=(0,0,1;0rad)
  diameter = 4
  invert = false
  leftHanded = false
  length = 2
  lengthCustom = 8
  matchOuter = false
  offset = 0
  thread = false
  type = 48
FEATURE [Part::FeaturePython] Screw001  label="M3x8-Screw001"  # Fasteners workbench fastener (typed FeaturePython)
  Placement = pos=(6,-19,3) rot=(0,0,1;0rad)
  diameter = 4
  invert = false
  leftHanded = false
  length = 2
  lengthCustom = 8
  matchOuter = false
  offset = 0
  thread = false
  type = 48
FEATURE [Part::Cylinder] Cylinder006
  Angle = 360
  AttacherType = Attacher::AttachEngine3D
  FirstAngle = 0
  Height = 10
  Placement = pos=(6,19,-8) rot=(0,0,1;0rad)
  Radius = 1.195
  SecondAngle = 0
FEATURE [Part::Cylinder] Cylinder007
  Angle = 360
  AttacherType = Attacher::AttachEngine3D
  FirstAngle = 0
  Height = 10
  Placement = pos=(6,-19,-8) rot=(0,0,1;0rad)
  Radius = 1.195
  SecondAngle = 0
FEATURE [Part::MultiFuse] Fusion003
  Shapes = -> [Cylinder006,Cylinder007]
FEATURE [Part::Cut] Cut003  label="Kickeraligner_01"
  Base = -> Cut002
  Tool = -> Fusion003
FEATURE [Part::Cylinder] Cylinder008
  Angle = 360
  AttacherType = Attacher::AttachEngine3D
  FirstAngle = 0
  Height = 10
  Placement = pos=(6,19,0) rot=(0,0,1;0rad)
  Radius = 1.7
  SecondAngle = 0
FEATURE [Part::Cylinder] Cylinder009
  Angle = 360
  AttacherType = Attacher::AttachEngine3D
  FirstAngle = 0
  Height = 10
  Placement = pos=(6,-19,0) rot=(0,0,1;0rad)
  Radius = 1.7
  SecondAngle = 0
FEATURE [Part::Cylinder] Cylinder010
  Angle = 360
  AttacherType = Attacher::AttachEngine3D
  FirstAngle = 0
  Height = 2
  Placement = pos=(6,19,3) rot=(0,0,1;0rad)
  Radius = 2.8
  SecondAngle = 0
FEATURE [Part::Cylinder] Cylinder011
  Angle = 360
  AttacherType = Attacher::AttachEngine3D
  FirstAngle = 0
  Height = 2
  Placement = pos=(6,-19,3) rot=(0,0,1;0rad)
  Radius = 2.8
  SecondAngle = 0
FEATURE [Part::MultiFuse] Fusion004
  Shapes = -> [Cylinder008,Cylinder009,Cylinder010,Cylinder011]
FEATURE [Part::Cut] Cut004
  Base = -> Cut
  Tool = -> Fusion004
FEATURE [Part::Cylinder] Cylinder012
  Angle = 360
  AttacherType = Attacher::AttachEngine3D
  FirstAngle = 0
  Height = 2
  Placement = pos=(0,0,3) rot=(0,0,1;0rad)
  Radius = 2.8
  SecondAngle = 0
FEATURE [Part::Cylinder] Cylinder013
  Angle = 360
  AttacherType = Attacher::AttachEngine3D
  FirstAngle = 0
  Height = 10
  Radius = 1.7
  SecondAngle = 0
FEATURE [Part::MultiFuse] Fusion005
  Shapes = -> [Cylinder013,Cylinder012]
FEATURE [Part::FeaturePython] Array  # Draft array (typed FeaturePython)
  AlwaysSyncPlacement = false
  Angle = 360
  ArrayType = 2
  Axis = (0,0,1)
  Base = -> Fusion005
  Center = (0,0,0)
  Count = 9
  ExpandArray = false
  Fuse = false
  IntervalAxis = (0,0,0)
  IntervalX = (100,0,0)
  IntervalY = (0,100,0)
  IntervalZ = (0,0,100)
  NumberCircles = 2
  NumberPolar = 5
  NumberX = 2
  NumberY = 2
  NumberZ = 1
  PlacementList = 9 placements: [(0,0,0),(-20,0,0),(-14.1421,-14.1421,0),(-4.44089e-15,-20,0),(14.1421,-14.1421,0),(20,-2.44929e-15,0),(14.1421,14.1421,0),(4.44089e-15,20,0),(-14.1421,14.1421,0)]
  RadialDistance = 20
  ScaleList = (9) [(1,1,1),(1,1,1),(1,1,1),(1,1,1),(1,1,1),(1,1,1),(1,1,1),(1,1,1),(1,1,1)]
  Symmetry = 1
  TangentialDistance = 15
FEATURE [Part::Cut] Cut005  label="AligningRing"
  Base = -> Cut004
  Tool = -> Array
FEATURE [Part::Feature] Cut005_solid  label="AligningRing (Solid)"
  shape: bbox 48 x 48 x 5 mm, 34 faces (baked)
FEATURE [TechDraw::DrawSVGTemplate] Template
  EditableTexts = Designed_by_Name=Thomas Spielauer; FC-Date=2024-06-04; FC-SC=mm; FC-Title=XL30 Column Alignment Ring; Subtitle=Subtitle
  Height = 210
  Orientation = 1
  Template = <path>
  Width = 297
FEATURE [TechDraw::DrawProjGroupItem] ProjItem  label="Front"
  CoarseView = false
  Direction = (0,0,1)
  Focus = 100
  HardHidden = false
  IsoCount = 0
  IsoHidden = false
  IsoVisible = false
  LockPosition = true
  Perspective = false
  Rotation = 0
  RotationVector = (0,1,0)
  Scale = 2
  ScaleType = 2
  ScrubCount = 0
  SeamHidden = false
  SeamVisible = false
  SmoothHidden = false
  SmoothVisible = true
  Source = -> [Cut005]
  Type = 0
  X = 0
  XDirection = (0,1,0)
  Y = 0
FEATURE [TechDraw::DrawProjGroupItem] ProjItem001  label="Rear"
  CoarseView = false
  Direction = (0,0,-1)
  Focus = 100
  HardHidden = false
  IsoCount = 0
  IsoHidden = false
  IsoVisible = false
  LockPosition = false
  Perspective = false
  Rotation = 0
  RotationVector = (1,0,0)
  Scale = 2
  ScaleType = 2
  ScrubCount = 0
  SeamHidden = false
  SeamVisible = false
  SmoothHidden = false
  SmoothVisible = true
  Source = -> [Cut005]
  Type = 3
  X = 136
  XDirection = (0,-1,0)
  Y = 0
FEATURE [TechDraw::DrawProjGroupItem] ProjItem002  label="Left"
  CoarseView = false
  Direction = (0,-1,1e-16)
  Focus = 100
  HardHidden = false
  IsoCount = 0
  IsoHidden = false
  IsoVisible = false
  LockPosition = false
  Perspective = false
  Rotation = 0
  RotationVector = (1,0,0)
  Scale = 2
  ScaleType = 2
  ScrubCount = 0
  SeamHidden = false
  SeamVisible = false
  SmoothHidden = false
  SmoothVisible = true
  Source = -> [Cut005]
  Type = 1
  X = 68
  XDirection = (0,1e-16,1)
  Y = 0
FEATURE [TechDraw::DrawProjGroup] ProjGroup
  Anchor = -> ProjItem
  AutoDistribute = true
  LockPosition = false
  ProjectionType = 0
  Rotation = 0
  Scale = 2
  ScaleType = 1
  Source = -> [Cut005]
  Views = -> [ProjItem,ProjItem001,ProjItem002]
  X = 75.1959
  Y = 130.904
  spacingX = 15
  spacingY = 15
FEATURE [TechDraw::DrawViewDimension] Dimension
  AngleOverride = false
  Arbitrary = false
  ArbitraryTolerances = false
  EqualTolerance = true
  ExtensionAngle = 0
  FormatSpec = %.2w
  FormatSpecOverTolerance = %+.2w
  FormatSpecUnderTolerance = %+.2w
  Inverted = false
  LineAngle = 0
  LockPosition = false
  MeasureType = 1
  OverTolerance = 0
  References2D = -> [ProjItem002]
  Rotation = 0
  ScaleType = 0
  TheoreticalExact = false
  Type = 1
  UnderTolerance = 0
  X = 14.6766
  Y = 64.1241
FEATURE [TechDraw::DrawViewDimension] Dimension001
  AngleOverride = false
  Arbitrary = false
  ArbitraryTolerances = false
  EqualTolerance = true
  ExtensionAngle = 0
  FormatSpec = ⌀%.2w
  FormatSpecOverTolerance = %+.2w
  FormatSpecUnderTolerance = %+.2w
  Inverted = false
  LineAngle = 0
  LockPosition = false
  MeasureType = 1
  OverTolerance = 0
  References2D = -> [ProjItem001]
  Rotation = 0
  ScaleType = 0
  TheoreticalExact = false
  Type = 5
  UnderTolerance = 0
  X = 14.4966
  Y = 59.5959
FEATURE [TechDraw::DrawViewDimension] Dimension002
  AngleOverride = false
  Arbitrary = false
  ArbitraryTolerances = false
  EqualTolerance = true
  ExtensionAngle = 0
  FormatSpec = ⌀%.2w
  FormatSpecOverTolerance = %+.2w
  FormatSpecUnderTolerance = %+.2w
  Inverted = false
  LineAngle = 0
  LockPosition = false
  MeasureType = 1
  OverTolerance = 0
  References2D = -> [ProjItem001]
  Rotation = 0
  ScaleType = 0
  TheoreticalExact = false
  Type = 5
  UnderTolerance = 0
  X = 30.1939
  Y = 53.0714
FEATURE [TechDraw::DrawViewDimension] Dimension003
  AngleOverride = false
  Arbitrary = false
  ArbitraryTolerances = false
  EqualTolerance = true
  ExtensionAngle = 0
  FormatSpec = ⌀%.2w (10x)
  FormatSpecOverTolerance = %+.2w
  FormatSpecUnderTolerance = %+.2w
  Inverted = false
  LineAngle = 0
  LockPosition = false
  MeasureType = 1
  OverTolerance = 0
  References2D = -> [ProjItem001]
  Rotation = 0
  ScaleType = 0
  TheoreticalExact = false
  Type = 5
  UnderTolerance = 0
  X = 49.7609
  Y = 51.7571
FEATURE [TechDraw::DrawViewDimension] Dimension004
  AngleOverride = false
  Arbitrary = false
  ArbitraryTolerances = false
  EqualTolerance = true
  ExtensionAngle = 0
  FormatSpec = ⌀%.2w
  FormatSpecOverTolerance = %+.2w
  FormatSpecUnderTolerance = %+.2w
  Inverted = false
  LineAngle = 0
  LockPosition = false
  MeasureType = 1
  OverTolerance = 0
  References2D = -> [ProjItem]
  Rotation = 0
  ScaleType = 0
  TheoreticalExact = false
  Type = 5
  UnderTolerance = 0
  X = 33.9204
  Y = 57.7895
FEATURE [TechDraw::DrawViewDimension] Dimension005
  AngleOverride = false
  Arbitrary = false
  ArbitraryTolerances = false
  EqualTolerance = true
  ExtensionAngle = 0
  FormatSpec = ⌀%.2w
  FormatSpecOverTolerance = %+.2w
  FormatSpecUnderTolerance = %+.2w
  Inverted = false
  LineAngle = 0
  LockPosition = false
  MeasureType = 1
  OverTolerance = 0
  References2D = -> [ProjItem]
  Rotation = 0
  ScaleType = 0
  TheoreticalExact = false
  Type = 5
  UnderTolerance = 0
  X = 26.899
  Y = 61.6719
FEATURE [TechDraw::DrawViewDimension] Dimension006
  AngleOverride = false
  Arbitrary = false
  ArbitraryTolerances = false
  EqualTolerance = true
  ExtensionAngle = 0
  FormatSpec = ⌀%.2w
  FormatSpecOverTolerance = %+.2w
  FormatSpecUnderTolerance = %+.2w
  Inverted = false
  LineAngle = 0
  LockPosition = false
  MeasureType = 1
  OverTolerance = 0
  References2D = -> [ProjItem]
  Rotation = 0
  ScaleType = 0
  TheoreticalExact = false
  Type = 5
  UnderTolerance = 0
  X = 17.5465
  Y = 63.697
FEATURE [TechDraw::DrawViewDimension] Dimension007
  AngleOverride = false
  Arbitrary = false
  ArbitraryTolerances = false
  EqualTolerance = true
  ExtensionAngle = 0
  FormatSpec = ⌀%.2w (10x)
  FormatSpecOverTolerance = %+.2w
  FormatSpecUnderTolerance = %+.2w
  Inverted = false
  LineAngle = 0
  LockPosition = false
  MeasureType = 1
  OverTolerance = 0
  References2D = -> [ProjItem]
  Rotation = 0
  ScaleType = 0
  TheoreticalExact = false
  Type = 5
  UnderTolerance = 0
  X = 45.3319
  Y = 51.7849
FEATURE [TechDraw::DrawViewDimension] Dimension008
  AngleOverride = false
  Arbitrary = false
  ArbitraryTolerances = false
  EqualTolerance = true
  ExtensionAngle = 0
  FormatSpec = ⌀%.2w
  FormatSpecOverTolerance = %+.2w
  FormatSpecUnderTolerance = %+.2w
  Inverted = false
  LineAngle = 0
  LockPosition = false
  MeasureType = 1
  OverTolerance = 0
  References2D = -> [ProjItem]
  Rotation = 0
  ScaleType = 0
  TheoreticalExact = false
  Type = 5
  UnderTolerance = 0
  X = -16.0753
  Y = 61.592
FEATURE [TechDraw::DrawViewDimension] Dimension009
  AngleOverride = false
  Arbitrary = false
  ArbitraryTolerances = false
  EqualTolerance = true
  ExtensionAngle = 0
  FormatSpec = %.2w (8x)
  FormatSpecOverTolerance = %+.2w
  FormatSpecUnderTolerance = %+.2w
  Inverted = false
  LineAngle = 0
  LockPosition = false
  MeasureType = 1
  OverTolerance = 0
  References2D = -> [ProjItem]
  Rotation = 0
  ScaleType = 0
  TheoreticalExact = false
  Type = 6
  UnderTolerance = 0
  X = -52.7672
  Y = 29.4701
FEATURE [TechDraw::DrawViewDimension] Dimension010
  AngleOverride = false
  Arbitrary = false
  ArbitraryTolerances = false
  EqualTolerance = true
  ExtensionAngle = 0
  FormatSpec = %.2w (2x)
  FormatSpecOverTolerance = %+.2w
  FormatSpecUnderTolerance = %+.2w
  Inverted = false
  LineAngle = 0
  LockPosition = false
  MeasureType = 1
  OverTolerance = 0
  References2D = -> [ProjItem]
  Rotation = 0
  ScaleType = 0
  TheoreticalExact = false
  Type = 6
  UnderTolerance = 0
  X = -41.0402
  Y = -30.1439
FEATURE [TechDraw::DrawViewSection] SectionView  label="Section  - "
  BaseView = -> ProjItem
  CoarseView = false
  CutSurfaceDisplay = 2
  Direction = (1e-16,-1,0)
  FileGeomPattern = <path>
  FileHatchPattern = <path>
  Focus = 100
  FuseBeforeCut = false
  HardHidden = false
  HatchOffset = (0,0,0)
  HatchRotation = 0
  HatchScale = 1
  IsoCount = 0
  IsoHidden = false
  IsoVisible = false
  LockPosition = false
  NameGeomPattern = Diamond
  Perspective = false
  Rotation = 0
  Scale = 2
  ScaleType = 2
  ScrubCount = 0
  SeamHidden = false
  SeamVisible = false
  SectionDirection = 4
  SectionLineStretch = 1
  SectionNormal = (1e-16,-1,0)
  SectionOrigin = (0,0,2.5)
  SmoothHidden = false
  SmoothVisible = true
  Source = -> [Cut005]
  TrimAfterCut = false
  UsePreviousCut = false
  X = 78.0601
  XDirection = (1,1e-16,0)
  Y = 34.3268
FEATURE [TechDraw::DrawViewDimension] Dimension011
  AngleOverride = false
  Arbitrary = false
  ArbitraryTolerances = false
  EqualTolerance = true
  ExtensionAngle = 0
  FormatSpec = %.2w
  FormatSpecOverTolerance = %+.2w
  FormatSpecUnderTolerance = %+.2w
  Inverted = false
  LineAngle = 0
  LockPosition = false
  MeasureType = 1
  OverTolerance = 0
  References2D = -> [SectionView]
  Rotation = 0
  ScaleType = 0
  TheoreticalExact = false
  Type = 2
  UnderTolerance = 0
  X = -56.9152
  Y = 17.9756
FEATURE [TechDraw::DrawViewDimension] Dimension012
  AngleOverride = false
  Arbitrary = false
  ArbitraryTolerances = false
  EqualTolerance = true
  ExtensionAngle = 0
  FormatSpec = %.2w
  FormatSpecOverTolerance = %+.2w
  FormatSpecUnderTolerance = %+.2w
  Inverted = false
  LineAngle = 0
  LockPosition = false
  MeasureType = 1
  OverTolerance = 0
  References2D = -> [SectionView]
  Rotation = 0
  ScaleType = 0
  TheoreticalExact = false
  Type = 2
  UnderTolerance = 0
  X = 51.4914
  Y = 16.9401
FEATURE [TechDraw::DrawViewDimension] Dimension013
  AngleOverride = false
  Arbitrary = false
  ArbitraryTolerances = false
  EqualTolerance = true
  ExtensionAngle = 0
  FormatSpec = %.2w
  FormatSpecOverTolerance = %+.2w
  FormatSpecUnderTolerance = %+.2w
  Inverted = false
  LineAngle = 0
  LockPosition = false
  MeasureType = 1
  OverTolerance = 0
  References2D = -> [SectionView]
  Rotation = 0
  ScaleType = 0
  TheoreticalExact = false
  Type = 1
  UnderTolerance = 0
  X = -1.79985
  Y = 16.369
FEATURE [TechDraw::DrawViewDimension] Dimension014
  AngleOverride = false
  Arbitrary = false
  ArbitraryTolerances = false
  EqualTolerance = true
  ExtensionAngle = 0
  FormatSpec = %.2w
  FormatSpecOverTolerance = %+.2w
  FormatSpecUnderTolerance = %+.2w
  Inverted = false
  LineAngle = 0
  LockPosition = false
  MeasureType = 1
  OverTolerance = 0
  References2D = -> [SectionView]
  Rotation = 0
  ScaleType = 0
  TheoreticalExact = false
  Type = 1
  UnderTolerance = 0
  X = -1.61231
  Y = -11.4713
FEATURE [TechDraw::DrawViewDimension] Dimension016
  AngleOverride = false
  Arbitrary = false
  ArbitraryTolerances = false
  EqualTolerance = true
  ExtensionAngle = 0
  FormatSpec = %.2w
  FormatSpecOverTolerance = %+.2w
  FormatSpecUnderTolerance = %+.2w
  Inverted = false
  LineAngle = 0
  LockPosition = false
  MeasureType = 1
  OverTolerance = 0
  References2D = -> [SectionView]
  Rotation = 0
  ScaleType = 0
  TheoreticalExact = false
  Type = 1
  UnderTolerance = 0
  X = -50.6255
  Y = -9.92308
FEATURE [TechDraw::DrawViewDimension] Dimension017
  AngleOverride = false
  Arbitrary = false
  ArbitraryTolerances = false
  EqualTolerance = true
  ExtensionAngle = 0
  FormatSpec = %.2w
  FormatSpecOverTolerance = %+.2w
  FormatSpecUnderTolerance = %+.2w
  Inverted = false
  LineAngle = 0
  LockPosition = false
  MeasureType = 1
  OverTolerance = 0
  References2D = -> [SectionView]
  Rotation = 0
  ScaleType = 0
  TheoreticalExact = false
  Type = 1
  UnderTolerance = 0
  X = -39.3802
  Y = 21.6146
FEATURE [TechDraw::DrawViewDimension] Dimension018
  AngleOverride = false
  Arbitrary = false
  ArbitraryTolerances = false
  EqualTolerance = true
  ExtensionAngle = 0
  FormatSpec = %.2w
  FormatSpecOverTolerance = %+.2w
  FormatSpecUnderTolerance = %+.2w
  Inverted = false
  LineAngle = 0
  LockPosition = false
  MeasureType = 1
  OverTolerance = 0
  References2D = -> [SectionView]
  Rotation = 0
  ScaleType = 0
  TheoreticalExact = false
  Type = 6
  UnderTolerance = 0
  X = 23.2977
  Y = -7.15191
FEATURE [TechDraw::DrawPage] Page
  KeepUpdated = true
  NextBalloonIndex = 1
  ProjectionType = 0
  Template = -> Template
  Views = -> [ProjGroup,Dimension,Dimension001,Dimension002,Dimension003,Dimension004,Dimension005,Dimension006,Dimension007,Dimension008,Dimension009,Dimension010,SectionView,Dimension011,Dimension012,Dimension013,Dimension014,Dimension016,Dimension017,Dimension018]
FEATURE [TechDraw::DrawSVGTemplate] Template001
  EditableTexts = Designed_by_Name=Thomas Spielauer; FC-Date=2024-06-04; FC-SC=mm; FC-Title=XL30 Kicker v3 Aligner; Subtitle=for Column aligning ring
  Height = 210
  Orientation = 1
  Template = <path>
  Width = 297
FEATURE [Part::Box] Box003  label="Cube003"
  AttacherType = Attacher::AttachEngine3D
  Height = 1.6
  Length = 12.5
  Placement = pos=(0,-2,0) rot=(0,0,1;0rad)
  Width = 4
FEATURE [Part::Cylinder] Cylinder014
  Angle = 360
  AttacherType = Attacher::AttachEngine3D
  FirstAngle = 0
  Height = 1.6
  Radius = 2
  SecondAngle = 0
FEATURE [Part::Cylinder] Cylinder015
  Angle = 360
  AttacherType = Attacher::AttachEngine3D
  FirstAngle = 0
  Height = 1.6
  Placement = pos=(12.6,0,0) rot=(0,0,1;0rad)
  Radius = 2
  SecondAngle = 0
FEATURE [Part::MultiFuse] Fusion006  label="Langloch002"
  Placement = pos=(7,-5.75,-7.7) rot=(0,1,0;1.5708rad)
  Shapes = -> [Box003,Cylinder014,Cylinder015]
FEATURE [Part::Box] Box004  label="Cube004"
  AttacherType = Attacher::AttachEngine3D
  Height = 1.6
  Length = 12.5
  Placement = pos=(0,-2,0) rot=(0,0,1;0rad)
  Width = 4
FEATURE [Part::Cylinder] Cylinder016
  Angle = 360
  AttacherType = Attacher::AttachEngine3D
  FirstAngle = 0
  Height = 1.6
  Radius = 2
  SecondAngle = 0
FEATURE [Part::Cylinder] Cylinder017
  Angle = 360
  AttacherType = Attacher::AttachEngine3D
  FirstAngle = 0
  Height = 1.6
  Placement = pos=(12.6,0,0) rot=(0,0,1;0rad)
  Radius = 2
  SecondAngle = 0
FEATURE [Part::MultiFuse] Fusion007  label="Langloch003"
  Placement = pos=(7,5.75,-7.7) rot=(0,1,0;1.5708rad)
  Shapes = -> [Box004,Cylinder016,Cylinder017]
FEATURE [Part::MultiFuse] Fusion008
  Shapes = -> [Fusion007,Fusion006]
FEATURE [Part::Cut] Cut006  label="Kickeraligner"
  Base = -> Cut003
  Tool = -> Fusion008
FEATURE [Part::Feature] Cut006_solid  label="Kickeraligner (Solid)"
  shape: bbox 5 x 44 x 25 mm, 60 faces (baked)
FEATURE [TechDraw::DrawProjGroupItem] ProjItem003  label="Front001"
  CoarseView = false
  Direction = (1,0,0)
  Focus = 100
  HardHidden = false
  IsoCount = 0
  IsoHidden = false
  IsoVisible = false
  LockPosition = true
  Perspective = false
  Rotation = 0
  RotationVector = (0,-1,0)
  Scale = 1.5
  ScaleType = 2
  ScrubCount = 0
  SeamHidden = false
  SeamVisible = false
  SmoothHidden = false
  SmoothVisible = true
  Source = -> [Cut006_solid]
  Type = 0
  X = 0
  XDirection = (0,-1,0)
  Y = 0
FEATURE [TechDraw::DrawProjGroupItem] ProjItem004  label="Bottom"
  CoarseView = false
  Direction = (0,0,1)
  Focus = 100
  HardHidden = false
  IsoCount = 0
  IsoHidden = false
  IsoVisible = false
  LockPosition = false
  Perspective = false
  Rotation = 0
  RotationVector = (1,0,0)
  Scale = 1.5
  ScaleType = 2
  ScrubCount = 0
  SeamHidden = false
  SeamVisible = false
  SmoothHidden = false
  SmoothVisible = true
  Source = -> [Cut006_solid]
  Type = 5
  X = 0
  XDirection = (0,-1,0)
  Y = 59.7197
FEATURE [TechDraw::DrawProjGroupItem] ProjItem005  label="Top"
  CoarseView = false
  Direction = (0,0,-1)
  Focus = 100
  HardHidden = false
  IsoCount = 0
  IsoHidden = false
  IsoVisible = false
  LockPosition = false
  Perspective = false
  Rotation = 0
  RotationVector = (1,0,0)
  Scale = 1.5
  ScaleType = 2
  ScrubCount = 0
  SeamHidden = false
  SeamVisible = false
  SmoothHidden = false
  SmoothVisible = true
  Source = -> [Cut006_solid]
  Type = 4
  X = 0
  XDirection = (0,-1,0)
  Y = -66.6557
FEATURE [TechDraw::DrawProjGroupItem] ProjItem006  label="Left001"
  CoarseView = false
  Direction = (1e-16,1,0)
  Focus = 100
  HardHidden = false
  IsoCount = 0
  IsoHidden = false
  IsoVisible = false
  LockPosition = false
  Perspective = false
  Rotation = 0
  RotationVector = (1,0,0)
  Scale = 1.5
  ScaleType = 2
  ScrubCount = 0
  SeamHidden = false
  SeamVisible = false
  SmoothHidden = false
  SmoothVisible = true
  Source = -> [Cut006_solid]
  Type = 1
  X = 84.3121
  XDirection = (1,-1e-16,0)
  Y = 0
FEATURE [TechDraw::DrawProjGroupItem] ProjItem007  label="Rear001"
  CoarseView = false
  Direction = (-1,0,0)
  Focus = 100
  HardHidden = false
  IsoCount = 0
  IsoHidden = false
  IsoVisible = false
  LockPosition = false
  Perspective = false
  Rotation = 0
  RotationVector = (1,0,0)
  Scale = 1.5
  ScaleType = 2
  ScrubCount = 0
  SeamHidden = false
  SeamVisible = false
  SmoothHidden = false
  SmoothVisible = true
  Source = -> [Cut006_solid]
  Type = 3
  X = 151.913
  XDirection = (0,1,0)
  Y = 0
FEATURE [TechDraw::DrawProjGroup] ProjGroup001
  Anchor = -> ProjItem003
  AutoDistribute = false
  LockPosition = false
  ProjectionType = 0
  Rotation = 0
  Scale = 1.5
  ScaleType = 1
  Source = -> [Cut006_solid]
  Views = -> [ProjItem003,ProjItem004,ProjItem005,ProjItem006,ProjItem007]
  X = 71.7176
  Y = 109.819
  spacingX = 15
  spacingY = 15
FEATURE [TechDraw::DrawViewDimension] Dimension019
  AngleOverride = false
  Arbitrary = false
  ArbitraryTolerances = false
  EqualTolerance = true
  ExtensionAngle = 0
  FormatSpec = %.2w
  FormatSpecOverTolerance = %+.2w
  FormatSpecUnderTolerance = %+.2w
  Inverted = false
  LineAngle = 0
  LockPosition = false
  MeasureType = 1
  OverTolerance = 0
  References2D = -> [ProjItem005]
  Rotation = 0
  ScaleType = 0
  TheoreticalExact = false
  Type = 0
  UnderTolerance = 0
  X = -2.74227
  Y = 17.7496
FEATURE [TechDraw::DrawViewDimension] Dimension020
  AngleOverride = false
  Arbitrary = false
  ArbitraryTolerances = false
  EqualTolerance = true
  ExtensionAngle = 0
  FormatSpec = %.2w
  FormatSpecOverTolerance = %+.2w
  FormatSpecUnderTolerance = %+.2w
  Inverted = false
  LineAngle = 0
  LockPosition = false
  MeasureType = 1
  OverTolerance = 0
  References2D = -> [ProjItem005]
  Rotation = 0
  ScaleType = 0
  TheoreticalExact = false
  Type = 0
  UnderTolerance = 0
  X = -42.4052
  Y = 17.6073
FEATURE [TechDraw::DrawViewDimension] Dimension021
  AngleOverride = false
  Arbitrary = false
  ArbitraryTolerances = false
  EqualTolerance = true
  ExtensionAngle = 0
  FormatSpec = %.2w
  FormatSpecOverTolerance = %+.2w
  FormatSpecUnderTolerance = %+.2w
  Inverted = false
  LineAngle = 0
  LockPosition = false
  MeasureType = 1
  OverTolerance = 0
  References2D = -> [ProjItem004]
  Rotation = 0
  ScaleType = 0
  TheoreticalExact = false
  Type = 0
  UnderTolerance = 0
  X = 38.6315
  Y = 21.9645
FEATURE [TechDraw::DrawViewDimension] Dimension022
  AngleOverride = false
  Arbitrary = false
  ArbitraryTolerances = false
  EqualTolerance = true
  ExtensionAngle = 0
  FormatSpec = %.2w
  FormatSpecOverTolerance = %+.2w
  FormatSpecUnderTolerance = %+.2w
  Inverted = false
  LineAngle = 0
  LockPosition = false
  MeasureType = 1
  OverTolerance = 0
  References2D = -> [ProjItem004]
  Rotation = 0
  ScaleType = 0
  TheoreticalExact = false
  Type = 0
  UnderTolerance = 0
  X = 44.0976
  Y = 10.1057
FEATURE [TechDraw::DrawViewDimension] Dimension023
  AngleOverride = false
  Arbitrary = false
  ArbitraryTolerances = false
  EqualTolerance = true
  ExtensionAngle = 0
  FormatSpec = ⌀%.2w (2x M3)
  FormatSpecOverTolerance = %+.2w
  FormatSpecUnderTolerance = %+.2w
  Inverted = false
  LineAngle = 0
  LockPosition = false
  MeasureType = 1
  OverTolerance = 0
  References2D = -> [ProjItem004]
  Rotation = 0
  ScaleType = 0
  TheoreticalExact = false
  Type = 5
  UnderTolerance = 0
  X = -49.8518
  Y = -22.963
FEATURE [TechDraw::DrawViewDimension] Dimension024
  AngleOverride = false
  Arbitrary = false
  ArbitraryTolerances = false
  EqualTolerance = true
  ExtensionAngle = 0
  FormatSpec = %.2w
  FormatSpecOverTolerance = %+.2w
  FormatSpecUnderTolerance = %+.2w
  Inverted = false
  LineAngle = 0
  LockPosition = false
  MeasureType = 1
  OverTolerance = 0
  References2D = -> [ProjItem003]
  Rotation = 0
  ScaleType = 0
  TheoreticalExact = false
  Type = 0
  UnderTolerance = 0
  X = 26.1719
  Y = 34.0957
FEATURE [TechDraw::DrawViewDimension] Dimension025
  AngleOverride = false
  Arbitrary = false
  ArbitraryTolerances = false
  EqualTolerance = true
  ExtensionAngle = 0
  FormatSpec = %.2w
  FormatSpecOverTolerance = %+.2w
  FormatSpecUnderTolerance = %+.2w
  Inverted = false
  LineAngle = 0
  LockPosition = false
  MeasureType = 1
  OverTolerance = 0
  References2D = -> [ProjItem003]
  Rotation = 0
  ScaleType = 0
  TheoreticalExact = false
  Type = 0
  UnderTolerance = 0
  X = 29.3359
  Y = 42.2976
FEATURE [TechDraw::DrawViewDimension] Dimension026
  AngleOverride = false
  Arbitrary = false
  ArbitraryTolerances = false
  EqualTolerance = true
  ExtensionAngle = 0
  FormatSpec = %.2w
  FormatSpecOverTolerance = %+.2w
  FormatSpecUnderTolerance = %+.2w
  Inverted = false
  LineAngle = 0
  LockPosition = false
  MeasureType = 1
  OverTolerance = 0
  References2D = -> [ProjItem003]
  Rotation = 0
  ScaleType = 0
  TheoreticalExact = false
  Type = 0
  UnderTolerance = 0
  X = 46.3655
  Y = 25.9377
FEATURE [TechDraw::DrawViewDimension] Dimension027
  AngleOverride = false
  Arbitrary = false
  ArbitraryTolerances = false
  EqualTolerance = true
  ExtensionAngle = 0
  FormatSpec = %.2w
  FormatSpecOverTolerance = %+.2w
  FormatSpecUnderTolerance = %+.2w
  Inverted = false
  LineAngle = 0
  LockPosition = false
  MeasureType = 1
  OverTolerance = 0
  References2D = -> [ProjItem003]
  Rotation = 0
  ScaleType = 0
  TheoreticalExact = false
  Type = 0
  UnderTolerance = 0
  X = 40.1856
  Y = 3.86506
FEATURE [TechDraw::DrawViewDimension] Dimension028
  AngleOverride = false
  Arbitrary = false
  ArbitraryTolerances = false
  EqualTolerance = true
  ExtensionAngle = 0
  FormatSpec = %.2w
  FormatSpecOverTolerance = %+.2w
  FormatSpecUnderTolerance = %+.2w
  Inverted = false
  LineAngle = 0
  LockPosition = false
  MeasureType = 1
  OverTolerance = 0
  References2D = -> [ProjItem003]
  Rotation = 0
  ScaleType = 0
  TheoreticalExact = false
  Type = 0
  UnderTolerance = 0
  X = -21.0897
  Y = 32.0725
FEATURE [TechDraw::DrawViewDimension] Dimension029
  AngleOverride = false
  Arbitrary = false
  ArbitraryTolerances = false
  EqualTolerance = true
  ExtensionAngle = 0
  FormatSpec = %.2w
  FormatSpecOverTolerance = %+.2w
  FormatSpecUnderTolerance = %+.2w
  Inverted = false
  LineAngle = 0
  LockPosition = false
  MeasureType = 1
  OverTolerance = 0
  References2D = -> [ProjItem007]
  Rotation = 0
  ScaleType = 0
  TheoreticalExact = false
  Type = 0
  UnderTolerance = 0
  X = 0.798609
  Y = 37.539
FEATURE [TechDraw::DrawViewDimension] Dimension030
  AngleOverride = false
  Arbitrary = false
  ArbitraryTolerances = false
  EqualTolerance = true
  ExtensionAngle = 0
  FormatSpec = %.2w
  FormatSpecOverTolerance = %+.2w
  FormatSpecUnderTolerance = %+.2w
  Inverted = false
  LineAngle = 0
  LockPosition = false
  MeasureType = 1
  OverTolerance = 0
  References2D = -> [ProjItem007]
  Rotation = 0
  ScaleType = 0
  TheoreticalExact = false
  Type = 0
  UnderTolerance = 0
  X = -2.99683
  Y = -30.5721
FEATURE [TechDraw::DrawViewDimension] Dimension031
  AngleOverride = false
  Arbitrary = false
  ArbitraryTolerances = false
  EqualTolerance = true
  ExtensionAngle = 0
  FormatSpec = %.2w
  FormatSpecOverTolerance = %+.2w
  FormatSpecUnderTolerance = %+.2w
  Inverted = false
  LineAngle = 0
  LockPosition = false
  MeasureType = 1
  OverTolerance = 0
  References2D = -> [ProjItem004]
  Rotation = 0
  ScaleType = 0
  TheoreticalExact = false
  Type = 0
  UnderTolerance = 0
  X = -28.8881
  Y = -11.5813
FEATURE [TechDraw::DrawViewDimension] Dimension032
  AngleOverride = false
  Arbitrary = false
  ArbitraryTolerances = false
  EqualTolerance = true
  ExtensionAngle = 0
  FormatSpec = %.2w
  FormatSpecOverTolerance = %+.2w
  FormatSpecUnderTolerance = %+.2w
  Inverted = false
  LineAngle = 0
  LockPosition = false
  MeasureType = 1
  OverTolerance = 0
  References2D = -> [ProjItem004]
  Rotation = 0
  ScaleType = 0
  TheoreticalExact = false
  Type = 0
  UnderTolerance = 0
  X = -1.50669
  Y = 20.5059
FEATURE [TechDraw::DrawPage] Page001
  KeepUpdated = true
  NextBalloonIndex = 1
  ProjectionType = 0
  Template = -> Template001
  Views = -> [ProjGroup001,Dimension019,Dimension020,Dimension021,Dimension022,Dimension023,Dimension024,Dimension025,Dimension026,Dimension027,Dimension028,Dimension029,Dimension030,Dimension031,Dimension032]
FEATURE [TechDraw::DrawSVGTemplate] Template002
  EditableTexts = Designed_by_Name=Designed by Name; Drawing_number=Drawing number; FC-Date=Date; FC-SC=Scale; FC-SH=Sheet; FC-Title=Title; Subtitle=Subtitle; Weight=Weight
  Height = 210
  Orientation = 1
  Template = <path>
  Width = 297
FEATURE [TechDraw::DrawViewPart] View
  CoarseView = false
  Direction = (1,0,0)
  Focus = 100
  HardHidden = false
  IsoCount = 0
  IsoHidden = false
  IsoVisible = false
  LockPosition = false
  Perspective = false
  Rotation = 0
  ScaleType = 0
  ScrubCount = 0
  SeamHidden = false
  SeamVisible = false
  SmoothHidden = false
  SmoothVisible = true
  Source = -> [Cut006_solid]
  X = 213.863
  XDirection = (0,-1,0)
  Y = 154.674
FEATURE [TechDraw::DrawViewPart] View001
  CoarseView = false
  Direction = (1,0,0)
  Focus = 100
  HardHidden = false
  IsoCount = 0
  IsoHidden = false
  IsoVisible = false
  LockPosition = false
  Perspective = false
  Rotation = 0
  ScaleType = 0
  ScrubCount = 0
  SeamHidden = false
  SeamVisible = false
  SmoothHidden = false
  SmoothVisible = true
  Source = -> [Cut006_solid]
  X = 76.3703
  XDirection = (0,-1,0)
  Y = 177.393
FEATURE [TechDraw::DrawViewSection] SectionView001  label="Section001  - "
  BaseView = -> View
  CoarseView = false
  CutSurfaceDisplay = 2
  Direction = (0,-1e-16,-1)
  FileGeomPattern = <path>
  FileHatchPattern = <path>
  Focus = 100
  FuseBeforeCut = false
  HardHidden = false
  HatchOffset = (0,0,0)
  HatchRotation = 0
  HatchScale = 1
  IsoCount = 0
  IsoHidden = false
  IsoVisible = false
  LockPosition = false
  NameGeomPattern = Diamond
  Perspective = false
  Rotation = 0
  Scale = 3
  ScaleType = 2
  ScrubCount = 0
  SeamHidden = false
  SeamVisible = false
  SectionDirection = 4
  SectionLineStretch = 1
  SectionNormal = (0,-1e-16,-1)
  SectionOrigin = (6,0,-12.5)
  SmoothHidden = false
  SmoothVisible = true
  Source = -> [Cut006_solid]
  TrimAfterCut = false
  UsePreviousCut = false
  X = 212.652
  XDirection = (0,-1,1e-16)
  Y = 93.0024
FEATURE [TechDraw::DrawViewDimension] Dimension033
  AngleOverride = false
  Arbitrary = false
  ArbitraryTolerances = false
  EqualTolerance = true
  ExtensionAngle = 0
  FormatSpec = %.2w
  FormatSpecOverTolerance = %+.2w
  FormatSpecUnderTolerance = %+.2w
  Inverted = false
  LineAngle = 0
  LockPosition = false
  MeasureType = 1
  OverTolerance = 0
  References2D = -> [SectionView001]
  Rotation = 0
  ScaleType = 0
  TheoreticalExact = false
  Type = 0
  UnderTolerance = 0
  X = 64.9192
  Y = -25.9707
FEATURE [TechDraw::DrawViewDimension] Dimension034
  AngleOverride = false
  Arbitrary = false
  ArbitraryTolerances = false
  EqualTolerance = true
  ExtensionAngle = 0
  FormatSpec = %.2w
  FormatSpecOverTolerance = %+.2w
  FormatSpecUnderTolerance = %+.2w
  Inverted = false
  LineAngle = 0
  LockPosition = false
  MeasureType = 1
  OverTolerance = 0
  References2D = -> [SectionView001]
  Rotation = 0
  ScaleType = 0
  TheoreticalExact = false
  Type = 0
  UnderTolerance = 0
  X = 66.5714
  Y = 28.6268
FEATURE [TechDraw::DrawViewDimension] Dimension035
  AngleOverride = false
  Arbitrary = false
  ArbitraryTolerances = false
  EqualTolerance = true
  ExtensionAngle = 0
  FormatSpec = %.2w
  FormatSpecOverTolerance = %+.2w
  FormatSpecUnderTolerance = %+.2w
  Inverted = false
  LineAngle = 0
  LockPosition = false
  MeasureType = 1
  OverTolerance = 0
  References2D = -> [SectionView001]
  Rotation = 0
  ScaleType = 0
  TheoreticalExact = false
  Type = 0
  UnderTolerance = 0
  X = 8.62255
  Y = -13.8392
FEATURE [TechDraw::DrawViewDimension] Dimension036
  AngleOverride = false
  Arbitrary = false
  ArbitraryTolerances = false
  EqualTolerance = true
  ExtensionAngle = 0
  FormatSpec = %.2w
  FormatSpecOverTolerance = %+.2w
  FormatSpecUnderTolerance = %+.2w
  Inverted = false
  LineAngle = 0
  LockPosition = false
  MeasureType = 1
  OverTolerance = 0
  References2D = -> [SectionView001]
  Rotation = 0
  ScaleType = 0
  TheoreticalExact = false
  Type = 0
  UnderTolerance = 0
  X = 47.3332
  Y = -18.2954
FEATURE [TechDraw::DrawViewSection] SectionView002  label="Section002  - "
  BaseView = -> View001
  CoarseView = false
  CutSurfaceDisplay = 2
  Direction = (0,-1e-16,-1)
  FileGeomPattern = <path>
  FileHatchPattern = <path>
  Focus = 100
  FuseBeforeCut = false
  HardHidden = false
  HatchOffset = (0,0,0)
  HatchRotation = 0
  HatchScale = 1
  IsoCount = 0
  IsoHidden = false
  IsoVisible = false
  LockPosition = false
  NameGeomPattern = Diamond
  Perspective = false
  Rotation = 0
  Scale = 3
  ScaleType = 2
  ScrubCount = 0
  SeamHidden = false
  SeamVisible = false
  SectionDirection = 4
  SectionLineStretch = 1
  SectionNormal = (0,-1e-16,-1)
  SectionOrigin = (6,0,-2.5)
  SmoothHidden = false
  SmoothVisible = true
  Source = -> [Cut006_solid]
  TrimAfterCut = false
  UsePreviousCut = false
  X = 79.6226
  XDirection = (0,-1,1e-16)
  Y = 118.575
FEATURE [TechDraw::DrawViewDimension] Dimension037
  AngleOverride = false
  Arbitrary = false
  ArbitraryTolerances = false
  EqualTolerance = true
  ExtensionAngle = 0
  FormatSpec = %.2w
  FormatSpecOverTolerance = %+.2w
  FormatSpecUnderTolerance = %+.2w
  Inverted = false
  LineAngle = 0
  LockPosition = false
  MeasureType = 1
  OverTolerance = 0
  References2D = -> [SectionView002]
  Rotation = 0
  ScaleType = 0
  TheoreticalExact = false
  Type = 0
  UnderTolerance = 0
  X = 0.325776
  Y = -3.69577
FEATURE [TechDraw::DrawViewDimension] Dimension038
  AngleOverride = false
  Arbitrary = false
  ArbitraryTolerances = false
  EqualTolerance = true
  ExtensionAngle = 0
  FormatSpec = %.2w
  FormatSpecOverTolerance = %+.2w
  FormatSpecUnderTolerance = %+.2w
  Inverted = false
  LineAngle = 0
  LockPosition = false
  MeasureType = 1
  OverTolerance = 0
  References2D = -> [SectionView002]
  Rotation = 0
  ScaleType = 0
  TheoreticalExact = false
  Type = 0
  UnderTolerance = 0
  X = 0.255463
  Y = 4.6556
FEATURE [TechDraw::DrawViewDimension] Dimension039
  AngleOverride = false
  Arbitrary = false
  ArbitraryTolerances = false
  EqualTolerance = true
  ExtensionAngle = 0
  FormatSpec = %.2w
  FormatSpecOverTolerance = %+.2w
  FormatSpecUnderTolerance = %+.2w
  Inverted = false
  LineAngle = 0
  LockPosition = false
  MeasureType = 1
  OverTolerance = 0
  References2D = -> [SectionView002]
  Rotation = 0
  ScaleType = 0
  TheoreticalExact = false
  Type = 0
  UnderTolerance = 0
  X = 79.5736
  Y = 0.671184
FEATURE [TechDraw::DrawViewDimension] Dimension040
  AngleOverride = false
  Arbitrary = false
  ArbitraryTolerances = false
  EqualTolerance = true
  ExtensionAngle = 0
  FormatSpec = ⌀%.2w (2x M3)
  FormatSpecOverTolerance = %+.2w
  FormatSpecUnderTolerance = %+.2w
  Inverted = false
  LineAngle = 0
  LockPosition = false
  MeasureType = 1
  OverTolerance = 0
  References2D = -> [SectionView002]
  Rotation = 0
  ScaleType = 0
  TheoreticalExact = false
  Type = 5
  UnderTolerance = 0
  X = 64.4898
  Y = 40.7105
FEATURE [TechDraw::DrawViewDimension] Dimension041
  AngleOverride = false
  Arbitrary = false
  ArbitraryTolerances = false
  EqualTolerance = true
  ExtensionAngle = 0
  FormatSpec = %.2w
  FormatSpecOverTolerance = %+.2w
  FormatSpecUnderTolerance = %+.2w
  Inverted = false
  LineAngle = 0
  LockPosition = false
  MeasureType = 1
  OverTolerance = 0
  References2D = -> [SectionView002]
  Rotation = 0
  ScaleType = 0
  TheoreticalExact = false
  Type = 0
  UnderTolerance = 0
  X = 78.1881
  Y = 8.43953
FEATURE [TechDraw::DrawViewDimension] Dimension042
  AngleOverride = false
  Arbitrary = false
  ArbitraryTolerances = false
  EqualTolerance = true
  ExtensionAngle = 0
  FormatSpec = R%.2w
  FormatSpecOverTolerance = %+.2w
  FormatSpecUnderTolerance = %+.2w
  Inverted = false
  LineAngle = 0
  LockPosition = false
  MeasureType = 1
  OverTolerance = 0
  References2D = -> [SectionView002]
  Rotation = 0
  ScaleType = 0
  TheoreticalExact = false
  Type = 4
  UnderTolerance = 0
  X = -21.5107
  Y = 13.7302
FEATURE [TechDraw::DrawViewDimension] Dimension043
  AngleOverride = false
  Arbitrary = false
  ArbitraryTolerances = false
  EqualTolerance = true
  ExtensionAngle = 0
  FormatSpec = %.2w
  FormatSpecOverTolerance = %+.2w
  FormatSpecUnderTolerance = %+.2w
  Inverted = false
  LineAngle = 0
  LockPosition = false
  MeasureType = 1
  OverTolerance = 0
  References2D = -> [SectionView002]
  Rotation = 0
  ScaleType = 0
  TheoreticalExact = false
  Type = 0
  UnderTolerance = 0
  X = 45.5158
  Y = 34.0796
FEATURE [TechDraw::DrawPage] Page002
  KeepUpdated = true
  NextBalloonIndex = 1
  ProjectionType = 0
  Template = -> Template002
  Views = -> [View,View001,SectionView001,Dimension033,Dimension034,Dimension035,Dimension036,SectionView002,Dimension037,Dimension038,Dimension039,Dimension040,Dimension041,Dimension042,Dimension043]
note: 9 file-system paths scrubbed to <path> (originals preserved in the JSON sidecar)
PROVENANCE & LICENSES
A FreeCAD (.FCStd) document from a public repository crawl; recipes are the document's own serialized feature recipes (and, for linked parts, companion documents' recipes).
License: bsd.
